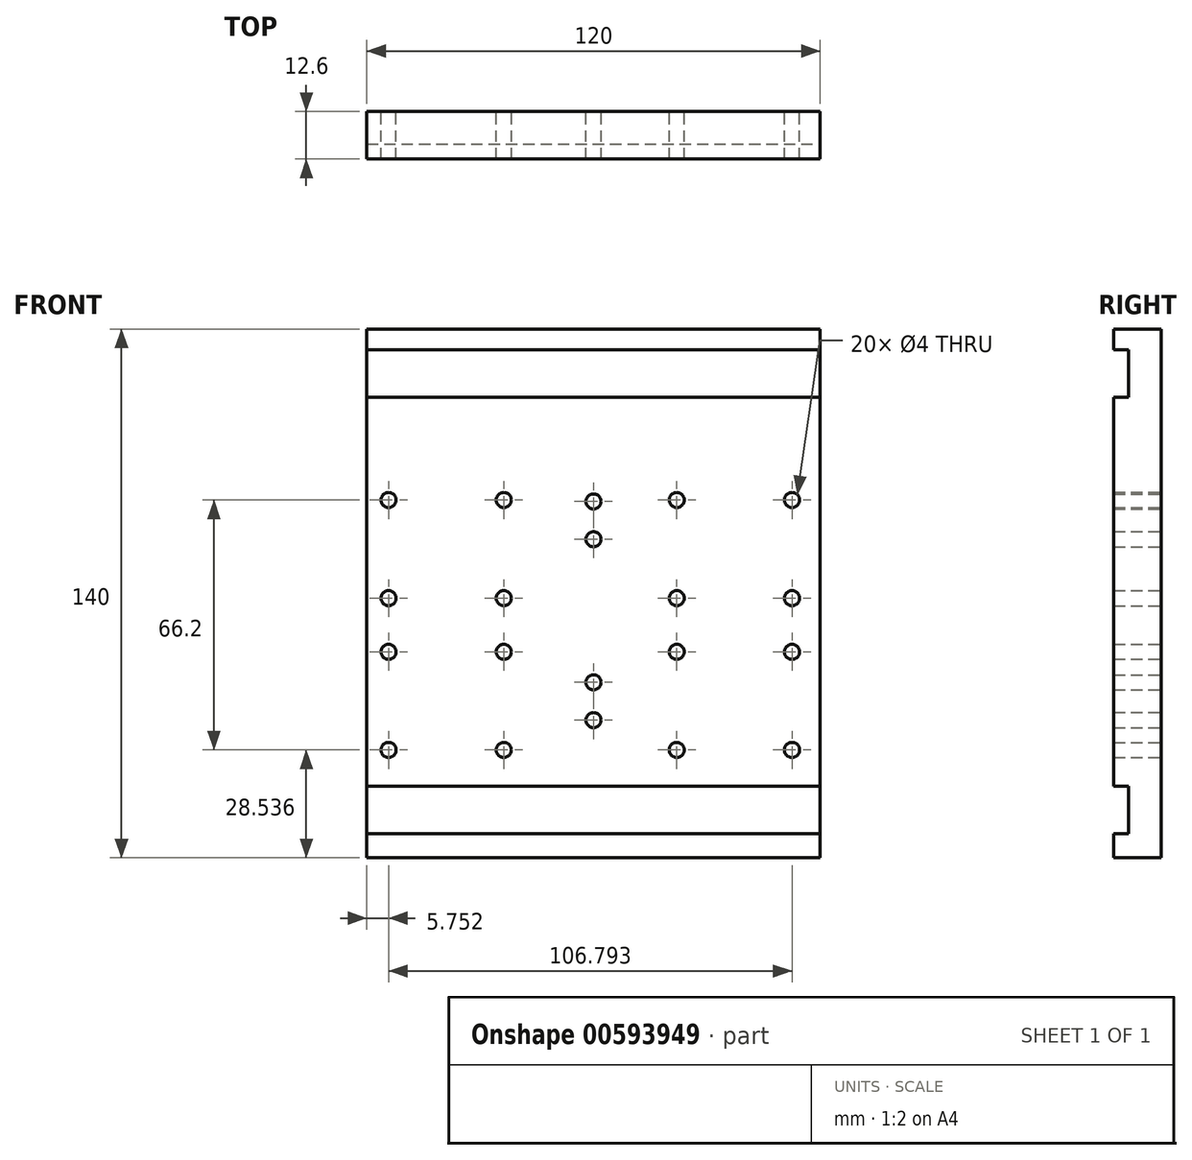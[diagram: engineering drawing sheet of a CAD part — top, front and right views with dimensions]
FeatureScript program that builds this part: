
annotation { "Feature Type Name" : "Feature", "Feature Type Description" : "" }
export const myFeature = defineFeature(function(context is Context, id is Id, definition is map)
    precondition{}
    {
        {
            var Q0;
            Q0=qCreatedBy(makeId("Front.planeOp"),FACE);
            var sketch = newSketch(context, id + "F0", { "sketchPlane" : qUnion([Q0])});
            skLineSegment(sketch, "E0.bottom", {"start": v(-8.87, 20.26) * mm, "end": v(-50.87, 20.26) * mm});
            skLineSegment(sketch, "E0.top", {"start": v(-8.87, 56.26) * mm, "end": v(-50.87, 56.26) * mm});
            skLineSegment(sketch, "E0.left", {"start": v(-8.87, 20.26) * mm, "end": v(-8.87, 56.26) * mm});
            skLineSegment(sketch, "E0.right", {"start": v(-50.87, 20.26) * mm, "end": v(-50.87, 56.26) * mm});
            skPoint(sketch, "E0.middle", {"position": v(-29.87, 38.26) * mm});
            skPoint(sketch, "E1.middle", {"position": v(-30.08, 37.78) * mm});
            skCircle(sketch, "E2", {"center": v(-45.12, 51.26) * mm, "radius": 2 * mm});
            skCircle(sketch, "E3.0.1.0", {"center": v(-45.12, 25.26) * mm, "radius": 2 * mm});
            skCircle(sketch, "E3.1.0.0", {"center": v(-14.62, 51.26) * mm, "radius": 2 * mm});
            skCircle(sketch, "E3.1.1.0", {"center": v(-14.62, 25.26) * mm, "radius": 2 * mm});
            skLineSegment(sketch, "E3.direction1", {"start": v(-45.12, 51.26) * mm, "end": v(-14.62, 51.26) * mm, "construction": true});
            skLineSegment(sketch, "E3.direction2", {"start": v(-45.12, 51.26) * mm, "end": v(-45.12, 25.26) * mm, "construction": true});
            skLineSegment(sketch, "E4.bottom", {"start": v(25.42, -19.94) * mm, "end": v(-34.58, -19.94) * mm});
            skLineSegment(sketch, "E4.top", {"start": v(-9.11, 16.16) * mm, "end": v(-50.87, 16.16) * mm});
            skLineSegment(sketch, "E4.left", {"start": v(-8.87, -19.94) * mm, "end": v(-8.87, 16.06) * mm});
            skLineSegment(sketch, "E4.right", {"start": v(-50.87, -19.94) * mm, "end": v(-50.87, 16.16) * mm});
            skCircle(sketch, "E5", {"center": v(-45.12, 11.06) * mm, "radius": 2 * mm});
            skCircle(sketch, "E6.0.1.0", {"center": v(-45.12, -14.94) * mm, "radius": 2 * mm});
            skCircle(sketch, "E6.1.0.0", {"center": v(-14.62, 11.06) * mm, "radius": 2 * mm});
            skCircle(sketch, "E6.1.1.0", {"center": v(-14.62, -14.94) * mm, "radius": 2 * mm});
            skLineSegment(sketch, "E6.direction1", {"start": v(-45.12, 11.06) * mm, "end": v(-14.62, 11.06) * mm, "construction": true});
            skLineSegment(sketch, "E6.direction2", {"start": v(-45.12, 11.06) * mm, "end": v(-45.12, -14.94) * mm, "construction": true});
            skCircle(sketch, "E7", {"center": v(9.13, 50.86) * mm, "radius": 2 * mm});
            skCircle(sketch, "E8", {"center": v(9.13, 40.86) * mm, "radius": 2 * mm});
            skCircle(sketch, "E9", {"center": v(9.13, 2.96) * mm, "radius": 2 * mm});
            skCircle(sketch, "E10", {"center": v(9.13, -7.04) * mm, "radius": 2 * mm});
            skLineSegment(sketch, "E11.1.0.0", {"start": v(67.42, 56.26) * mm, "end": v(25.42, 56.26) * mm});
            skCircle(sketch, "E11.1.0.1", {"center": v(61.67, 25.26) * mm, "radius": 2 * mm});
            skLineSegment(sketch, "E11.1.0.2", {"start": v(31.17, 51.26) * mm, "end": v(61.67, 51.26) * mm, "construction": true});
            skLineSegment(sketch, "E11.1.0.3", {"start": v(31.17, 51.26) * mm, "end": v(31.17, 25.26) * mm, "construction": true});
            skLineSegment(sketch, "E11.1.0.4", {"start": v(67.42, -19.94) * mm, "end": v(67.42, 16.06) * mm});
            skLineSegment(sketch, "E11.1.0.5", {"start": v(67.42, 20.26) * mm, "end": v(67.42, 56.26) * mm});
            skLineSegment(sketch, "E11.1.0.6", {"start": v(69.13, 16.06) * mm, "end": v(25.42, 16.06) * mm});
            skLineSegment(sketch, "E11.1.0.7", {"start": v(31.17, 11.06) * mm, "end": v(61.67, 11.06) * mm, "construction": true});
            skPoint(sketch, "E11.1.0.8", {"position": v(46.22, 37.78) * mm});
            skLineSegment(sketch, "E11.1.0.9", {"start": v(25.42, 20.26) * mm, "end": v(25.42, 56.26) * mm});
            skCircle(sketch, "E11.1.0.10", {"center": v(31.17, 51.26) * mm, "radius": 2 * mm});
            skLineSegment(sketch, "E11.1.0.11", {"start": v(69.13, -19.94) * mm, "end": v(25.42, -19.94) * mm});
            skLineSegment(sketch, "E11.1.0.12", {"start": v(67.42, 20.26) * mm, "end": v(25.42, 20.26) * mm});
            skCircle(sketch, "E11.1.0.13", {"center": v(31.17, 25.26) * mm, "radius": 2 * mm});
            skCircle(sketch, "E11.1.0.14", {"center": v(31.17, -14.94) * mm, "radius": 2 * mm});
            skLineSegment(sketch, "E11.1.0.15", {"start": v(25.42, -19.94) * mm, "end": v(25.42, 16.06) * mm});
            skPoint(sketch, "E11.1.0.16", {"position": v(46.42, 38.26) * mm});
            skCircle(sketch, "E11.1.0.17", {"center": v(61.67, -14.94) * mm, "radius": 2 * mm});
            skLineSegment(sketch, "E11.1.0.18", {"start": v(31.17, 11.06) * mm, "end": v(31.17, -14.94) * mm, "construction": true});
            skCircle(sketch, "E11.1.0.19", {"center": v(61.67, 51.26) * mm, "radius": 2 * mm});
            skCircle(sketch, "E11.1.0.20", {"center": v(61.67, 11.06) * mm, "radius": 2 * mm});
            skCircle(sketch, "E11.1.0.21", {"center": v(31.17, 11.06) * mm, "radius": 2 * mm});
            skLineSegment(sketch, "E11.direction1", {"start": v(-50.87, -19.94) * mm, "end": v(9.13, -19.94) * mm, "construction": true});
            skLineSegment(sketch, "E12.bottom", {"start": v(-50.87, 96.52) * mm, "end": v(69.13, 96.52) * mm});
            skLineSegment(sketch, "E12.top", {"start": v(-50.87, -43.48) * mm, "end": v(69.13, -43.48) * mm});
            skLineSegment(sketch, "E12.left", {"start": v(-50.87, 96.52) * mm, "end": v(-50.87, -43.48) * mm});
            skLineSegment(sketch, "E12.right", {"start": v(69.13, 96.52) * mm, "end": v(69.13, -43.48) * mm});
            skLineSegment(sketch, "E13.bottom", {"start": v(-50.87, 91.1) * mm, "end": v(69.13, 91.1) * mm});
            skLineSegment(sketch, "E13.top", {"start": v(-50.87, 78.5) * mm, "end": v(69.13, 78.5) * mm});
            skLineSegment(sketch, "E13.left", {"start": v(-50.87, 74.17) * mm, "end": v(-50.87, 61.57) * mm});
            skLineSegment(sketch, "E13.right", {"start": v(69.13, 74.17) * mm, "end": v(69.13, 61.57) * mm});
            skLineSegment(sketch, "E14.bottom", {"start": v(69.13, -24.5) * mm, "end": v(-50.87, -24.5) * mm});
            skLineSegment(sketch, "E14.top", {"start": v(69.13, -37.1) * mm, "end": v(-50.87, -37.1) * mm});
            skLineSegment(sketch, "E14.left", {"start": v(69.13, -24.5) * mm, "end": v(69.13, -37.1) * mm});
            skLineSegment(sketch, "E14.right", {"start": v(-50.87, -24.5) * mm, "end": v(-50.87, -37.1) * mm});
            skSolve(sketch);
        }
        {
            var Q0;
            {var subQ1=sQuery(id+"F0.wireOp",EDGE,"E0.bottom");Q0=makeQuery(id+"F0.imprint","IMPRINT",FACE,{"disambiguationData":[TD([[makeQuery(id+"F0.imprint","IMPRINT",EDGE,{"derivedFrom":subQ1}),1.0]])]});}
            var Q1;
            {var subQ1=sQuery(id+"F0.wireOp",EDGE,"E0.bottom");Q1=makeQuery(id+"F0.imprint","IMPRINT",FACE,{"disambiguationData":[TD([[makeQuery(id+"F0.imprint","IMPRINT",EDGE,{"derivedFrom":subQ1}),-1.0]])]});}
            var Q2;
            {var subQ0=sQuery(id+"F0.wireOp",EDGE,"E11.1.0.0");Q2=makeQuery(id+"F0.imprint","IMPRINT",FACE,{"disambiguationData":[TD([[makeQuery(id+"F0.imprint","IMPRINT",EDGE,{"derivedFrom":subQ0}),1.0]])]});}
            var Q3;
            {var subQ1=sQuery(id+"F0.wireOp",EDGE,"E11.1.0.6");Q3=makeQuery(id+"F0.imprint","IMPRINT",FACE,{"disambiguationData":[TD([[makeQuery(id+"F0.imprint","IMPRINT",EDGE,{"derivedFrom":subQ1}),1.0]])]});}
            var Q4;
            {var subQ1=sQuery(id+"F0.wireOp",EDGE,"E4.bottom");Q4=makeQuery(id+"F0.imprint","IMPRINT",FACE,{"disambiguationData":[TD([[makeQuery(id+"F0.imprint","IMPRINT",EDGE,{"derivedFrom":subQ1}),-1.0]])]});}
            var Q5;
            {var subQ0=sQuery(id+"F0.wireOp",EDGE,"E12.bottom");Q5=makeQuery(id+"F0.imprint","IMPRINT",FACE,{"disambiguationData":[TD([[makeQuery(id+"F0.imprint","IMPRINT",EDGE,{"derivedFrom":subQ0}),-1.0]])]});}
            var Q6;
            {var subQ0=sQuery(id+"F0.wireOp",EDGE,"E12.top");Q6=makeQuery(id+"F0.imprint","IMPRINT",FACE,{"disambiguationData":[TD([[makeQuery(id+"F0.imprint","IMPRINT",EDGE,{"derivedFrom":subQ0}),1.0]])]});}
            var Q7;
            Q7=makeQuery(id+"F0.imprint","IMPRINT",FACE,{"disambiguationData":[TD([[makeQuery(id+"F0.imprint","IMPRINT",EDGE,{"derivedFrom":sQuery(id+"F0.wireOp",EDGE,"E13.bottom")}),-1.0]])]});
            var Q8;
            Q8=makeQuery(id+"F0.imprint","IMPRINT",FACE,{"disambiguationData":[TD([[makeQuery(id+"F0.imprint","IMPRINT",EDGE,{"derivedFrom":sQuery(id+"F0.wireOp",EDGE,"E14.bottom")}),1.0]])]});
            var Q9;
            {var subQ4=sQuery(id+"F0.wireOp",EDGE,"E4.bottom");Q9=makeQuery(id+"F0.imprint","IMPRINT",FACE,{"disambiguationData":[TD([[makeQuery(id+"F0.imprint","IMPRINT",EDGE,{"derivedFrom":subQ4}),1.0]])]});}
            var Q10;
            Q10=makeQuery(id+"F0.imprint","IMPRINT",FACE,{"disambiguationData":[TD([[makeQuery(id+"F0.imprint","IMPRINT",EDGE,{"derivedFrom":sQuery(id+"F0.wireOp",EDGE,"E11.1.0.1")}),-1.0]])]});
            var Q11;
            {var subQ2=sQuery(id+"F0.wireOp",EDGE,"E11.1.0.4");Q11=makeQuery(id+"F0.imprint","IMPRINT",FACE,{"disambiguationData":[TD([[makeQuery(id+"F0.imprint","IMPRINT",EDGE,{"derivedFrom":subQ2}),1.0]])]});}
            extrude(context, id + "F1", {"entities" : qUnion([Q0, Q1, Q2, Q3, Q4, Q5, Q6, Q7, Q8, Q9, Q10, Q11]), "depth" : 12.6 * mm, "offsetDistance" : 25 * mm});
        }
        {
            var Q0;
            Q0=makeQuery(id+"F1.opExtrude","CAP_FACE",FACE,{"disambiguationData":[OSD([sQuery(id+"F0.wireOp",EDGE,"E2"),sQuery(id+"F0.wireOp",EDGE,"E3.0.1.0"),sQuery(id+"F0.wireOp",EDGE,"E3.1.0.0"),sQuery(id+"F0.wireOp",EDGE,"E3.1.1.0"),sQuery(id+"F0.wireOp",EDGE,"E5"),sQuery(id+"F0.wireOp",EDGE,"E6.0.1.0"),sQuery(id+"F0.wireOp",EDGE,"E6.1.0.0"),sQuery(id+"F0.wireOp",EDGE,"E6.1.1.0"),sQuery(id+"F0.wireOp",EDGE,"E7"),sQuery(id+"F0.wireOp",EDGE,"E8"),sQuery(id+"F0.wireOp",EDGE,"E9"),sQuery(id+"F0.wireOp",EDGE,"E10"),sQuery(id+"F0.wireOp",EDGE,"E11.1.0.1"),sQuery(id+"F0.wireOp",EDGE,"E11.1.0.10"),sQuery(id+"F0.wireOp",EDGE,"E11.1.0.13"),sQuery(id+"F0.wireOp",EDGE,"E11.1.0.14"),sQuery(id+"F0.wireOp",EDGE,"E11.1.0.17"),sQuery(id+"F0.wireOp",EDGE,"E11.1.0.19"),sQuery(id+"F0.wireOp",EDGE,"E11.1.0.20"),sQuery(id+"F0.wireOp",EDGE,"E11.1.0.21"),sQuery(id+"F0.wireOp",EDGE,"E12.bottom"),sQuery(id+"F0.wireOp",EDGE,"E12.top"),sQuery(id+"F0.wireOp",EDGE,"E12.left"),sQuery(id+"F0.wireOp",EDGE,"E12.right"),sQuery(id+"F0.wireOp",EDGE,"E13.left"),sQuery(id+"F0.wireOp",EDGE,"E13.right"),sQuery(id+"F0.wireOp",EDGE,"E14.left"),sQuery(id+"F0.wireOp",EDGE,"E14.right")])],"isStart":false});
            var sketch = newSketch(context, id + "F2", { "sketchPlane" : qUnion([Q0])});
            skLineSegment(sketch, "E15.bottom", {"start": v(-50.87, 91.03) * mm, "end": v(69.13, 91.03) * mm});
            skLineSegment(sketch, "E15.top", {"start": v(-50.87, 78.43) * mm, "end": v(69.13, 78.43) * mm});
            skLineSegment(sketch, "E15.left", {"start": v(-50.87, 74.01) * mm, "end": v(-50.87, 61.46) * mm});
            skLineSegment(sketch, "E15.right", {"start": v(69.13, 74.01) * mm, "end": v(69.13, 61.46) * mm});
            skLineSegment(sketch, "E16.bottom", {"start": v(-50.87, -24.57) * mm, "end": v(69.13, -24.57) * mm});
            skLineSegment(sketch, "E16.top", {"start": v(-50.87, -37.17) * mm, "end": v(69.13, -37.17) * mm});
            skLineSegment(sketch, "E16.left", {"start": v(-50.87, -24.57) * mm, "end": v(-50.87, -37.17) * mm});
            skLineSegment(sketch, "E16.right", {"start": v(69.13, -24.57) * mm, "end": v(69.13, -37.17) * mm});
            skSolve(sketch);
        }
        {
            var Q0;
            Q0=makeQuery(id+"F2.imprint","IMPRINT",FACE,{"disambiguationData":[TD([[makeQuery(id+"F2.imprint","IMPRINT",EDGE,{"derivedFrom":sQuery(id+"F2.wireOp",EDGE,"E15.bottom")}),-1.0]])]});
            var Q1;
            Q1=makeQuery(id+"F2.imprint","IMPRINT",FACE,{"disambiguationData":[TD([[makeQuery(id+"F2.imprint","IMPRINT",EDGE,{"derivedFrom":sQuery(id+"F2.wireOp",EDGE,"E16.bottom")}),-1.0]])]});
            extrude(context, id + "F3", {"entities" : qUnion([Q0, Q1]), "operationType" : NewBodyOperationType.REMOVE, "oppositeDirection" : true, "depth" : 4 * mm, "offsetDistance" : 25 * mm});
        }
    });
